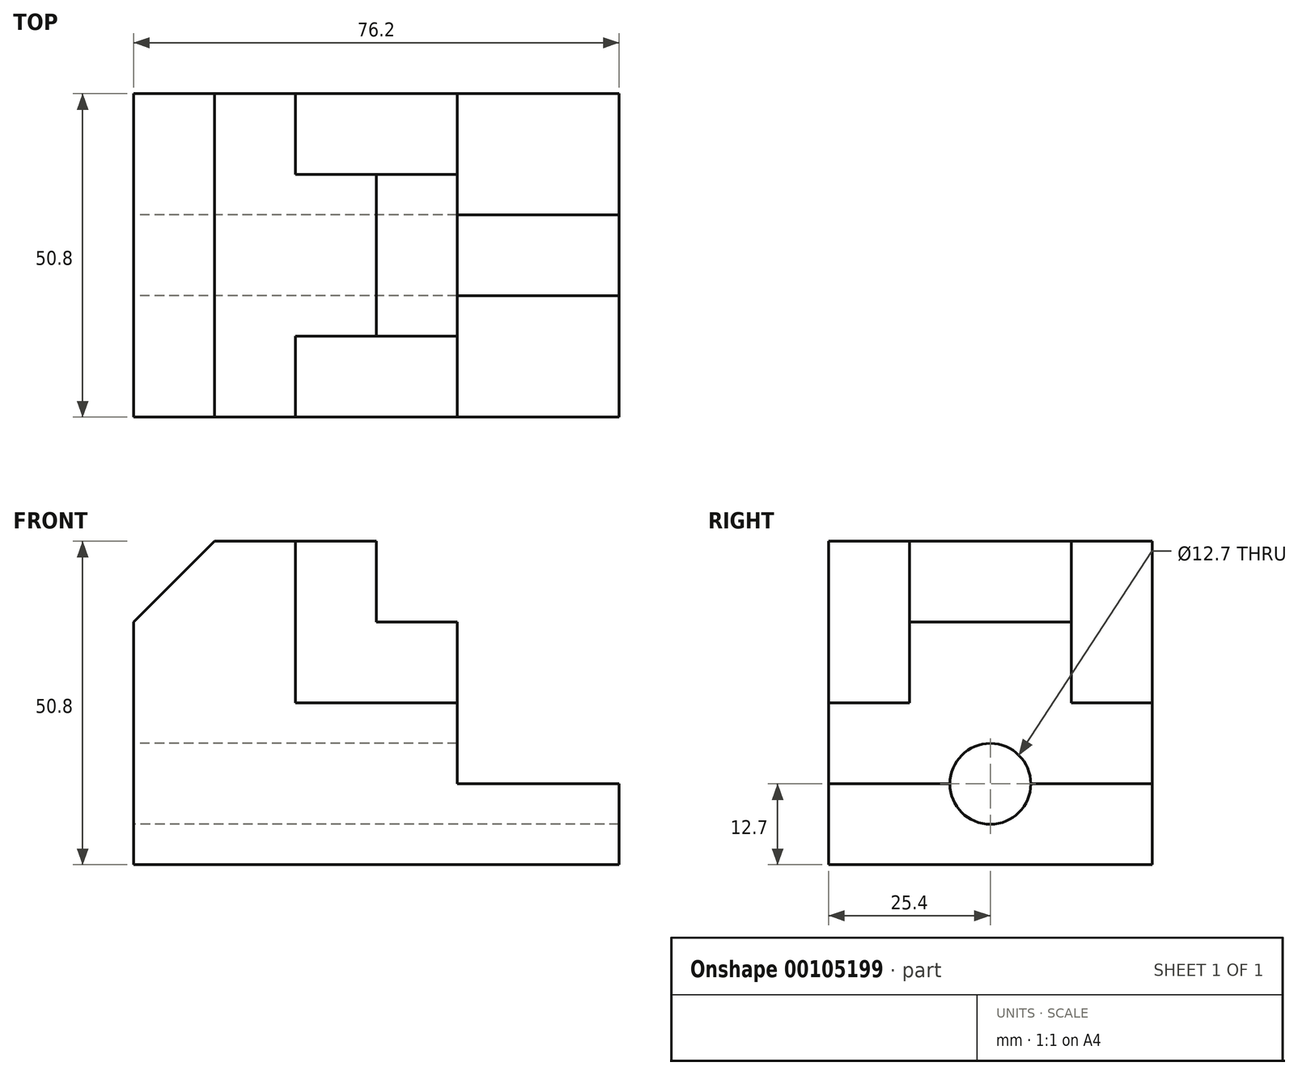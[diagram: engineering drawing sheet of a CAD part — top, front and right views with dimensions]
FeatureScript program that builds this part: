
annotation { "Feature Type Name" : "Feature", "Feature Type Description" : "" }
export const myFeature = defineFeature(function(context is Context, id is Id, definition is map)
    precondition{}
    {
        {
            var Q0;
            Q0=qCreatedBy(makeId("Front.planeOp"),FACE);
            var sketch = newSketch(context, id + "F0", { "sketchPlane" : qUnion([Q0])});
            skLineSegment(sketch, "E0", {"start": v(0, 0) * mm, "end": v(76.2, 0) * mm});
            skLineSegment(sketch, "E1", {"start": v(0, 0) * mm, "end": v(0, 38.1) * mm});
            skLineSegment(sketch, "E2", {"start": v(0, 38.1) * mm, "end": v(0, 50.8) * mm});
            skLineSegment(sketch, "E3", {"start": v(0, 50.8) * mm, "end": v(25.4, 50.8) * mm});
            skLineSegment(sketch, "E4", {"start": v(25.4, 50.8) * mm, "end": v(25.4, 25.4) * mm});
            skLineSegment(sketch, "E5", {"start": v(25.4, 25.4) * mm, "end": v(50.8, 25.4) * mm});
            skLineSegment(sketch, "E6", {"start": v(50.8, 25.4) * mm, "end": v(50.8, 12.7) * mm});
            skLineSegment(sketch, "E7", {"start": v(50.8, 12.7) * mm, "end": v(76.2, 12.7) * mm});
            skLineSegment(sketch, "E8", {"start": v(76.2, 12.7) * mm, "end": v(76.2, 0) * mm});
            skLineSegment(sketch, "E9", {"start": v(0, 38.1) * mm, "end": v(12.7, 50.8) * mm});
            skLineSegment(sketch, "E10", {"start": v(12.7, 50.8) * mm, "end": v(0, 50.8) * mm});
            skSolve(sketch);
        }
        {
            var Q0;
            Q0 = qSketchRegion(id + "F0", true);
            extrude(context, id + "F1", {"entities" : qUnion([Q0]), "endBound" : BoundingType.SYMMETRIC, "depth" : 50.8 * mm});
        }
        {
            var Q0;
            Q0=qCreatedBy(makeId("Top.planeOp"),FACE);
            var sketch = newSketch(context, id + "F2", { "sketchPlane" : qUnion([Q0])});
            skLineSegment(sketch, "E11", {"start": v(25.4, 12.7) * mm, "end": v(38.1, 12.7) * mm});
            skLineSegment(sketch, "E12", {"start": v(38.1, 12.7) * mm, "end": v(38.1, -12.7) * mm});
            skLineSegment(sketch, "E13", {"start": v(38.1, -12.7) * mm, "end": v(25.4, -12.7) * mm});
            skLineSegment(sketch, "E14", {"start": v(25.4, -12.7) * mm, "end": v(25.4, 12.7) * mm});
            skSolve(sketch);
        }
        {
            var Q0;
            Q0 = qSketchRegion(id + "F2", true);
            extrude(context, id + "F3", {"entities" : qUnion([Q0]), "operationType" : NewBodyOperationType.ADD, "depth" : 50.8 * mm});
        }
        {
            var Q0;
            Q0=qCreatedBy(makeId("Top.planeOp"),FACE);
            var sketch = newSketch(context, id + "F4", { "sketchPlane" : qUnion([Q0])});
            skLineSegment(sketch, "E15.bottom", {"start": v(38.1, 12.7) * mm, "end": v(50.8, 12.7) * mm});
            skLineSegment(sketch, "E15.top", {"start": v(38.1, -12.7) * mm, "end": v(50.8, -12.7) * mm});
            skLineSegment(sketch, "E15.left", {"start": v(38.1, 12.7) * mm, "end": v(38.1, -12.7) * mm});
            skLineSegment(sketch, "E15.right", {"start": v(50.8, 12.7) * mm, "end": v(50.8, -12.7) * mm});
            skSolve(sketch);
        }
        {
            var Q0;
            Q0 = qSketchRegion(id + "F4", true);
            extrude(context, id + "F5", {"entities" : qUnion([Q0]), "operationType" : NewBodyOperationType.ADD, "depth" : 38.1 * mm});
        }
        {
            var Q0;
            Q0=makeQuery(id+"F0.imprint","IMPRINT",FACE,{"disambiguationData":[TD([[makeQuery(id+"F0.imprint","IMPRINT",EDGE,{"derivedFrom":sQuery(id+"F0.wireOp",EDGE,"E2")}),-1.0]])]});
            extrude(context, id + "F6", {"entities" : qUnion([Q0]), "operationType" : NewBodyOperationType.REMOVE, "endBound" : BoundingType.THROUGH_ALL, "depth" : 25.4 * mm});
        }
        {
            var Q0;
            Q0=qCreatedBy(makeId("Front.planeOp"),FACE);
            var sketch = newSketch(context, id + "F7", { "sketchPlane" : qUnion([Q0])});
            skLineSegment(sketch, "E16", {"start": v(12.7, 50.8) * mm, "end": v(0, 38.1) * mm});
            skLineSegment(sketch, "E17", {"start": v(0, 38.1) * mm, "end": v(0, 50.8) * mm});
            skLineSegment(sketch, "E18", {"start": v(0, 50.8) * mm, "end": v(12.7, 50.8) * mm});
            skSolve(sketch);
        }
        {
            var Q0;
            Q0 = qSketchRegion(id + "F7", true);
            extrude(context, id + "F8", {"entities" : qUnion([Q0]), "operationType" : NewBodyOperationType.REMOVE, "endBound" : BoundingType.THROUGH_ALL, "oppositeDirection" : true, "depth" : 25.4 * mm});
        }
        {
            var Q0;
            Q0=qCreatedBy(makeId("Right.planeOp"),FACE);
            var sketch = newSketch(context, id + "F9", { "sketchPlane" : qUnion([Q0])});
            skCircle(sketch, "E19", {"center": v(0, 12.7) * mm, "radius": 6.35 * mm});
            skSolve(sketch);
        }
        {
            var Q0;
            Q0 = qSketchRegion(id + "F9", true);
            extrude(context, id + "F10", {"entities" : qUnion([Q0]), "operationType" : NewBodyOperationType.REMOVE, "endBound" : BoundingType.THROUGH_ALL, "depth" : 25.4 * mm});
        }
    });
